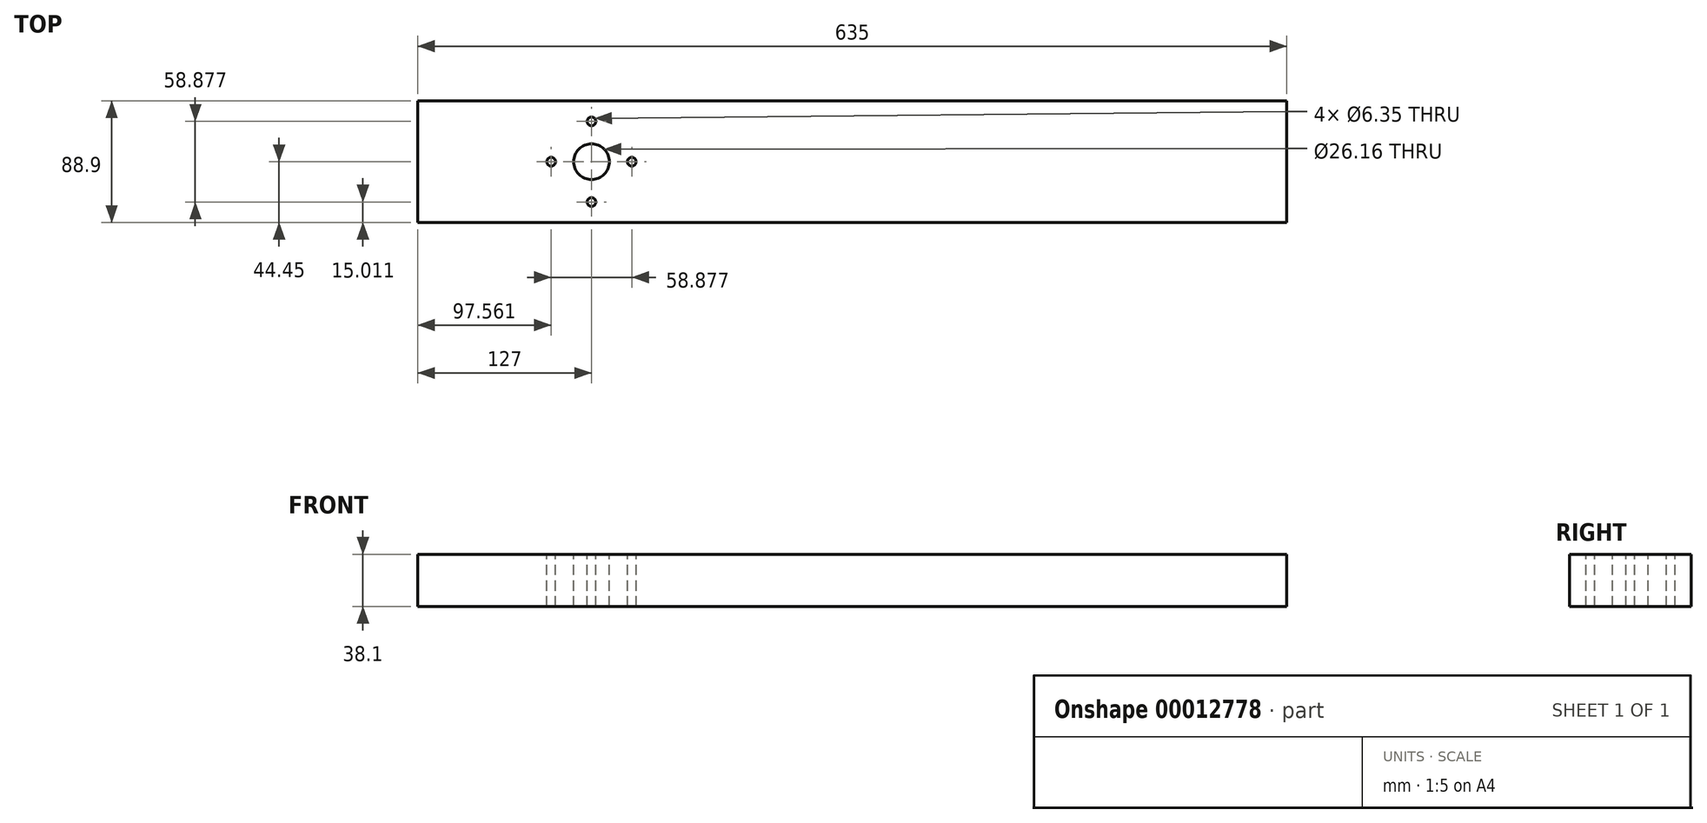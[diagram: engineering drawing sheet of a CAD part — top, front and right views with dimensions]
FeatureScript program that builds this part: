
annotation { "Feature Type Name" : "Feature", "Feature Type Description" : "" }
export const myFeature = defineFeature(function(context is Context, id is Id, definition is map)
    precondition{}
    {
        {
            var Q0;
            Q0=qCreatedBy(makeId("Right.planeOp"),FACE);
            var sketch = newSketch(context, id + "F0", { "sketchPlane" : qUnion([Q0])});
            skLineSegment(sketch, "E0.rect.bottom", {"start": v(44.45, 19.05) * mm, "end": v(-44.45, 19.05) * mm});
            skLineSegment(sketch, "E0.rect.top", {"start": v(44.45, -19.05) * mm, "end": v(-44.45, -19.05) * mm});
            skLineSegment(sketch, "E0.rect.left", {"start": v(44.45, 19.05) * mm, "end": v(44.45, -19.05) * mm});
            skLineSegment(sketch, "E0.rect.right", {"start": v(-44.45, 19.05) * mm, "end": v(-44.45, -19.05) * mm});
            skPoint(sketch, "E0.rect.middle", {"position": v(0, 0) * mm});
            skSolve(sketch);
        }
        {
            var Q0;
            Q0=makeQuery(id+"F0.imprint","IMPRINT",FACE,{"disambiguationData":[TD([[makeQuery(id+"F0.imprint","IMPRINT",EDGE,{"derivedFrom":sQuery(id+"F0.wireOp",EDGE,"E0.rect.bottom")}),1.0]])]});
            extrude(context, id + "F1", {"entities" : qUnion([Q0]), "depth" : 635 * mm});
        }
        {
            var Q0;
            Q0=makeQuery(id+"F1.opExtrude","SWEPT_FACE",FACE,{"disambiguationData":[OSD([sQuery(id+"F0.wireOp",EDGE,"E0.rect.bottom")])]});
            var sketch = newSketch(context, id + "F2", { "sketchPlane" : qUnion([Q0])});
            skCircle(sketch, "E1", {"center": v(127, 0) * mm, "radius": 13.08 * mm});
            skLineSegment(sketch, "E2", {"start": v(127, 0) * mm, "end": v(127, 29.44) * mm});
            skCircle(sketch, "E3", {"center": v(127, 29.44) * mm, "radius": 3.18 * mm});
            skCircle(sketch, "E4.1.0", {"center": v(97.56, 0) * mm, "radius": 3.18 * mm});
            skCircle(sketch, "E4.2.0", {"center": v(127, -29.44) * mm, "radius": 3.18 * mm});
            skCircle(sketch, "E5.1.3.0", {"center": v(156.44, 0) * mm, "radius": 3.18 * mm});
            skSolve(sketch);
        }
        {
            var Q0;
            Q0=makeQuery(id+"F2.imprint","IMPRINT",FACE,{"disambiguationData":[TD([[makeQuery(id+"F2.imprint","IMPRINT",EDGE,{"derivedFrom":sQuery(id+"F2.wireOp",EDGE,"E1")}),1.0]])]});
            var Q1;
            Q1=makeQuery(id+"F2.imprint","IMPRINT",FACE,{"disambiguationData":[TD([[makeQuery(id+"F2.imprint","IMPRINT",EDGE,{"derivedFrom":sQuery(id+"F2.wireOp",EDGE,"E4.2.0")}),1.0]])]});
            var Q2;
            Q2=makeQuery(id+"F2.imprint","IMPRINT",FACE,{"disambiguationData":[TD([[makeQuery(id+"F2.imprint","IMPRINT",EDGE,{"derivedFrom":sQuery(id+"F2.wireOp",EDGE,"E5.1.3.0")}),1.0]])]});
            var Q3;
            Q3=makeQuery(id+"F2.imprint","IMPRINT",FACE,{"disambiguationData":[TD([[makeQuery(id+"F2.imprint","IMPRINT",EDGE,{"derivedFrom":sQuery(id+"F2.wireOp",EDGE,"E3")}),1.0]])]});
            var Q4;
            Q4=makeQuery(id+"F2.imprint","IMPRINT",FACE,{"disambiguationData":[TD([[makeQuery(id+"F2.imprint","IMPRINT",EDGE,{"derivedFrom":sQuery(id+"F2.wireOp",EDGE,"E4.1.0")}),1.0]])]});
            var Q5;
            Q5=sQuery(id+"F2.wireOp",EDGE,"E1");
            var Q6;
            Q6=makeQuery(id+"F1.opExtrude","SWEPT_FACE",FACE,{"disambiguationData":[OSD([sQuery(id+"F0.wireOp",EDGE,"E0.rect.top")])]});
            extrude(context, id + "F3", {"entities" : qUnion([Q0, Q1, Q2, Q3, Q4]), "operationType" : NewBodyOperationType.REMOVE, "surfaceEntities" : qUnion([Q5]), "endBound" : BoundingType.UP_TO_SURFACE, "oppositeDirection" : true, "endBoundEntityFace" : qUnion([Q6]), "depth" : 25.4 * mm});
        }
    });
